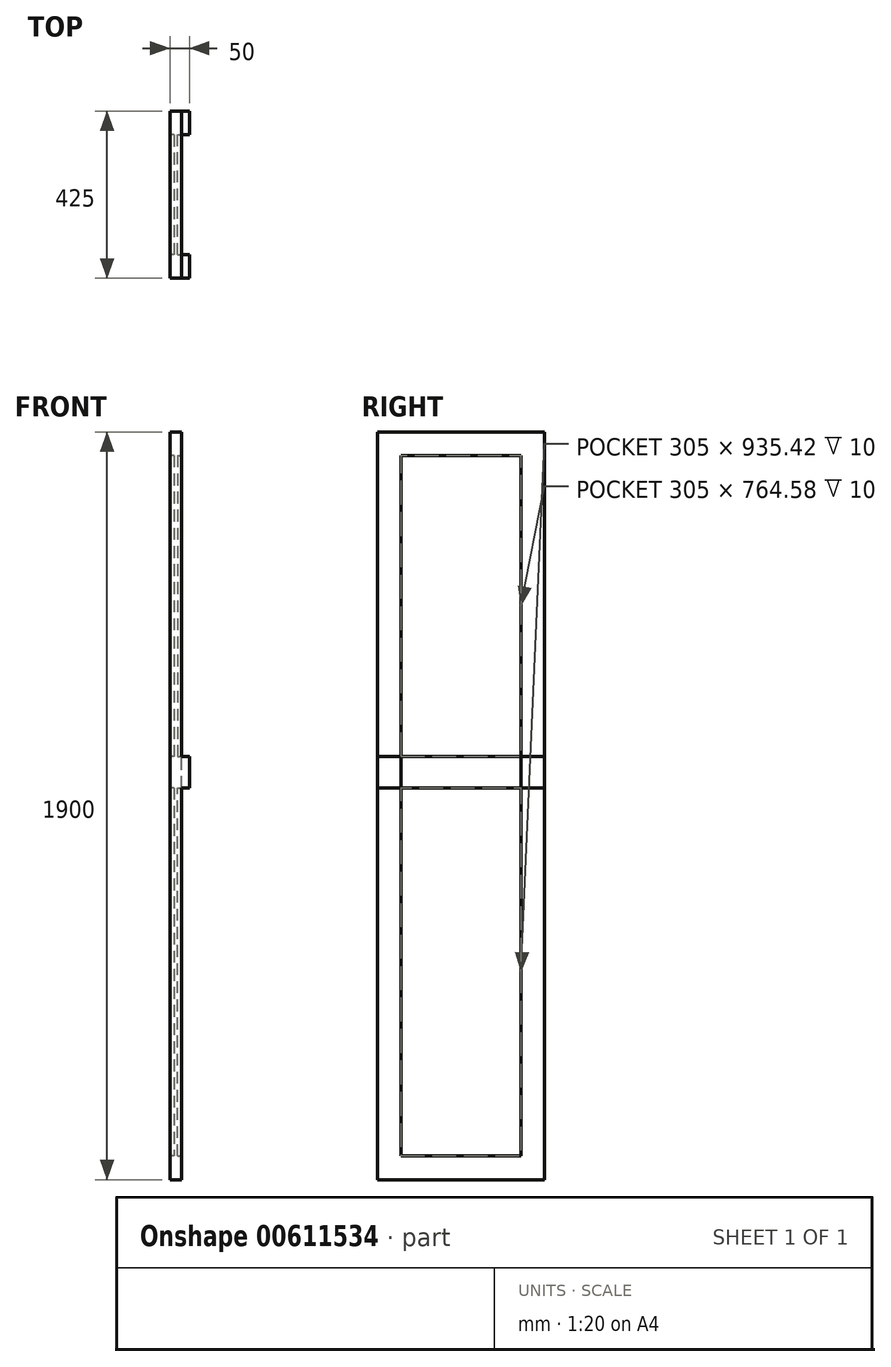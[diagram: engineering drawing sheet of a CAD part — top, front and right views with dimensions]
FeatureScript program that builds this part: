
annotation { "Feature Type Name" : "Feature", "Feature Type Description" : "" }
export const myFeature = defineFeature(function(context is Context, id is Id, definition is map)
    precondition{}
    {
        {
            var Q0;
            Q0=qCreatedBy(makeId("Right.planeOp"),FACE);
            var sketch = newSketch(context, id + "F0", { "sketchPlane" : qUnion([Q0])});
            skLineSegment(sketch, "E0.bottom", {"start": v(0, 0) * mm, "end": v(425, 0) * mm});
            skLineSegment(sketch, "E0.top", {"start": v(0, 1900) * mm, "end": v(425, 1900) * mm});
            skLineSegment(sketch, "E0.left", {"start": v(0, 0) * mm, "end": v(0, 1900) * mm});
            skLineSegment(sketch, "E0.right", {"start": v(425, 0) * mm, "end": v(425, 1900) * mm});
            skSolve(sketch);
        }
        {
            var Q0;
            Q0=makeQuery(id+"F0.imprint","IMPRINT",FACE,{"disambiguationData":[TD([[makeQuery(id+"F0.imprint","IMPRINT",EDGE,{"derivedFrom":sQuery(id+"F0.wireOp",EDGE,"E0.bottom")}),1.0]])]});
            extrude(context, id + "F1", {"entities" : qUnion([Q0]), "depth" : 30 * mm, "offsetDistance" : 25 * mm});
        }
        {
            var Q0;
            Q0=makeQuery(id+"F1.opExtrude","CAP_FACE",FACE,{"disambiguationData":[OSD([sQuery(id+"F0.wireOp",EDGE,"E0.bottom"),sQuery(id+"F0.wireOp",EDGE,"E0.top"),sQuery(id+"F0.wireOp",EDGE,"E0.left"),sQuery(id+"F0.wireOp",EDGE,"E0.right")])],"isStart":false});
            var sketch = newSketch(context, id + "F2", { "sketchPlane" : qUnion([Q0])});
            skLineSegment(sketch, "E1.bottom", {"start": v(60, 1840) * mm, "end": v(365, 1840) * mm});
            skLineSegment(sketch, "E1.top", {"start": v(60, 1075.42) * mm, "end": v(365, 1075.42) * mm});
            skLineSegment(sketch, "E1.left", {"start": v(60, 1840) * mm, "end": v(60, 1075.42) * mm});
            skLineSegment(sketch, "E1.right", {"start": v(365, 1840) * mm, "end": v(365, 1075.42) * mm});
            skLineSegment(sketch, "E2.bottom", {"start": v(60, 60) * mm, "end": v(365, 60) * mm});
            skLineSegment(sketch, "E2.top", {"start": v(60, 995.42) * mm, "end": v(365, 995.42) * mm});
            skLineSegment(sketch, "E2.left", {"start": v(60, 60) * mm, "end": v(60, 995.42) * mm});
            skLineSegment(sketch, "E2.right", {"start": v(365, 60) * mm, "end": v(365, 995.42) * mm});
            skSolve(sketch);
        }
        {
            var Q0;
            Q0=makeQuery(id+"F2.imprint","IMPRINT",FACE,{"disambiguationData":[TD([[makeQuery(id+"F2.imprint","IMPRINT",EDGE,{"derivedFrom":sQuery(id+"F2.wireOp",EDGE,"E1.bottom")}),-1.0]])]});
            var Q1;
            Q1=makeQuery(id+"F2.imprint","IMPRINT",FACE,{"disambiguationData":[TD([[makeQuery(id+"F2.imprint","IMPRINT",EDGE,{"derivedFrom":sQuery(id+"F2.wireOp",EDGE,"E2.bottom")}),1.0]])]});
            extrude(context, id + "F3", {"entities" : qUnion([Q0, Q1]), "operationType" : NewBodyOperationType.REMOVE, "oppositeDirection" : true, "depth" : 10 * mm, "offsetDistance" : 25 * mm});
        }
        {
            var Q0;
            Q0=makeQuery(id+"F1.opExtrude","CAP_FACE",FACE,{"disambiguationData":[OSD([sQuery(id+"F0.wireOp",EDGE,"E0.bottom"),sQuery(id+"F0.wireOp",EDGE,"E0.top"),sQuery(id+"F0.wireOp",EDGE,"E0.left"),sQuery(id+"F0.wireOp",EDGE,"E0.right")])],"isStart":true});
            var sketch = newSketch(context, id + "F4", { "sketchPlane" : qUnion([Q0])});
            skLineSegment(sketch, "E3.bottom", {"start": v(-60, 1840) * mm, "end": v(-365, 1840) * mm});
            skLineSegment(sketch, "E3.top", {"start": v(-60, 1075.42) * mm, "end": v(-365, 1075.42) * mm});
            skLineSegment(sketch, "E3.left", {"start": v(-365, 1840) * mm, "end": v(-365, 1075.42) * mm});
            skLineSegment(sketch, "E3.right", {"start": v(-60, 1840) * mm, "end": v(-60, 1075.42) * mm});
            skLineSegment(sketch, "E4.bottom", {"start": v(-365, 995.42) * mm, "end": v(-60, 995.42) * mm});
            skLineSegment(sketch, "E4.top", {"start": v(-365, 60) * mm, "end": v(-60, 60) * mm});
            skLineSegment(sketch, "E4.left", {"start": v(-365, 995.42) * mm, "end": v(-365, 60) * mm});
            skLineSegment(sketch, "E4.right", {"start": v(-60, 995.42) * mm, "end": v(-60, 60) * mm});
            skSolve(sketch);
        }
        {
            var Q0;
            Q0=qSketchRegion(id+"F4",true);
            extrude(context, id + "F5", {"entities" : qUnion([Q0]), "operationType" : NewBodyOperationType.REMOVE, "oppositeDirection" : true, "depth" : 10 * mm, "offsetDistance" : 25 * mm});
        }
        {
            var Q0;
            Q0=makeQuery(id+"F1.opExtrude","CAP_FACE",FACE,{"disambiguationData":[OSD([sQuery(id+"F0.wireOp",EDGE,"E0.bottom"),sQuery(id+"F0.wireOp",EDGE,"E0.top"),sQuery(id+"F0.wireOp",EDGE,"E0.left"),sQuery(id+"F0.wireOp",EDGE,"E0.right")])],"isStart":true});
            var sketch = newSketch(context, id + "F6", { "sketchPlane" : qUnion([Q0])});
            skLineSegment(sketch, "E5.bottom", {"start": v(-365, 1075.42) * mm, "end": v(-425, 1075.42) * mm});
            skLineSegment(sketch, "E5.top", {"start": v(-365, 995.42) * mm, "end": v(-425, 995.42) * mm});
            skLineSegment(sketch, "E5.left", {"start": v(-365, 1075.42) * mm, "end": v(-365, 995.42) * mm});
            skLineSegment(sketch, "E5.right", {"start": v(-425, 1075.42) * mm, "end": v(-425, 995.42) * mm});
            skLineSegment(sketch, "E6.bottom", {"start": v(-60, 1075.42) * mm, "end": v(0, 1075.42) * mm});
            skLineSegment(sketch, "E6.top", {"start": v(-60, 995.42) * mm, "end": v(0, 995.42) * mm});
            skLineSegment(sketch, "E6.left", {"start": v(-60, 1075.42) * mm, "end": v(-60, 995.42) * mm});
            skLineSegment(sketch, "E6.right", {"start": v(0, 1075.42) * mm, "end": v(0, 995.42) * mm});
            skSolve(sketch);
        }
        {
            var Q0;
            Q0=makeQuery(id+"F6.imprint","IMPRINT",FACE,{"disambiguationData":[TD([[makeQuery(id+"F6.imprint","IMPRINT",EDGE,{"derivedFrom":sQuery(id+"F6.wireOp",EDGE,"E5.bottom")}),1.0]])]});
            var Q1;
            Q1=makeQuery(id+"F6.imprint","IMPRINT",FACE,{"disambiguationData":[TD([[makeQuery(id+"F6.imprint","IMPRINT",EDGE,{"derivedFrom":sQuery(id+"F6.wireOp",EDGE,"E6.bottom")}),-1.0]])]});
            extrude(context, id + "F7", {"entities" : qUnion([Q0, Q1]), "operationType" : NewBodyOperationType.ADD, "oppositeDirection" : true, "depth" : 50 * mm, "offsetDistance" : 25 * mm});
        }
    });
